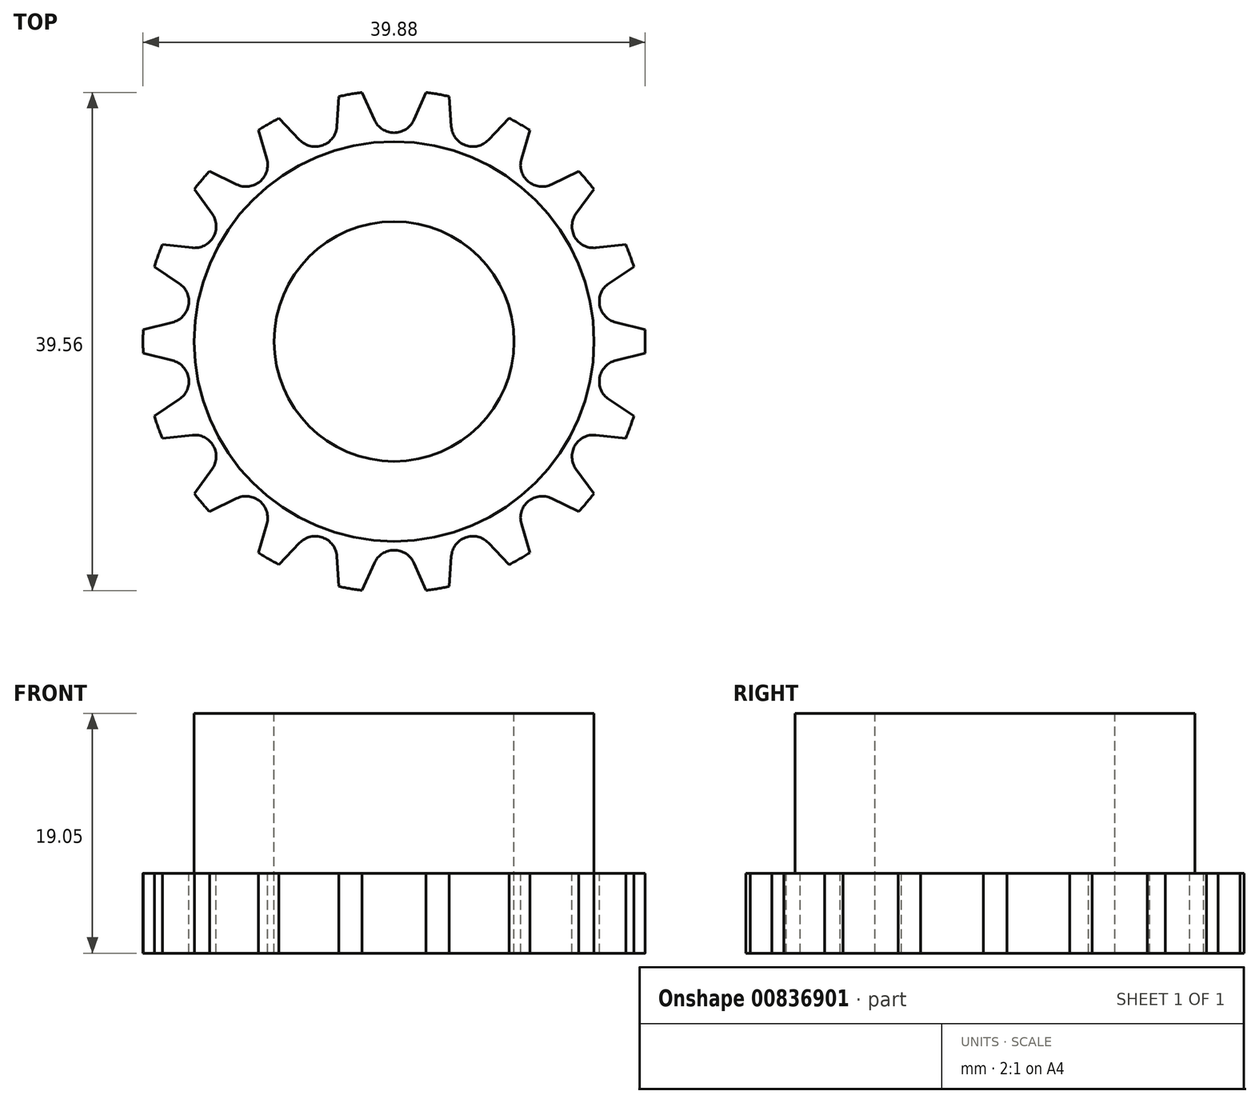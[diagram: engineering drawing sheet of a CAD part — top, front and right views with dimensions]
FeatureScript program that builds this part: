
annotation { "Feature Type Name" : "Feature", "Feature Type Description" : "" }
export const myFeature = defineFeature(function(context is Context, id is Id, definition is map)
    precondition{}
    {
        {
            var Q0;
            Q0=qCreatedBy(makeId("Top.planeOp"),FACE);
            var sketch = newSketch(context, id + "F0", { "sketchPlane" : qUnion([Q0])});
            skCircle(sketch, "E0", {"center": v(0, 0) * mm, "radius": 19.94 * mm});
            skSolve(sketch);
        }
        {
            var Q0;
            Q0=makeQuery(id+"F0.imprint","IMPRINT",FACE,{"disambiguationData":[TD([[makeQuery(id+"F0.imprint","IMPRINT",EDGE,{"derivedFrom":sQuery(id+"F0.wireOp",EDGE,"E0")}),1.0]])]});
            extrude(context, id + "F1", {"entities" : qUnion([Q0]), "depth" : 6.35 * mm, "offsetDistance" : 25.4 * mm});
        }
        {
            var Q0;
            Q0=makeQuery(id+"F1.opExtrude","CAP_FACE",FACE,{"disambiguationData":[OSD([sQuery(id+"F0.wireOp",EDGE,"E0")])],"isStart":false});
            var sketch = newSketch(context, id + "F2", { "sketchPlane" : qUnion([Q0])});
            skCircle(sketch, "E1", {"center": v(0, 0) * mm, "radius": 15.88 * mm});
            skSolve(sketch);
        }
        {
            var Q0;
            Q0 = qSketchRegion(id + "F2", true);
            extrude(context, id + "F3", {"entities" : qUnion([Q0]), "operationType" : NewBodyOperationType.ADD, "depth" : 12.7 * mm, "offsetDistance" : 25.4 * mm});
        }
        {
            var Q0;
            Q0=makeQuery(id+"F3.opExtrude","CAP_FACE",FACE,{"disambiguationData":[OSD([sQuery(id+"F2.wireOp",EDGE,"E1")])],"isStart":false});
            var sketch = newSketch(context, id + "F4", { "sketchPlane" : qUnion([Q0])});
            skCircle(sketch, "E2", {"center": v(0, 0) * mm, "radius": 9.53 * mm});
            skSolve(sketch);
        }
        {
            var Q0;
            Q0 = qSketchRegion(id + "F4", true);
            extrude(context, id + "F5", {"entities" : qUnion([Q0]), "operationType" : NewBodyOperationType.REMOVE, "oppositeDirection" : true, "depth" : 25.4 * mm, "offsetDistance" : 25.4 * mm});
        }
        {
            var Q0;
            Q0=makeQuery(id+"F1.opExtrude","CAP_FACE",FACE,{"disambiguationData":[OSD([sQuery(id+"F0.wireOp",EDGE,"E0")])],"isStart":false});
            var sketch = newSketch(context, id + "F6", { "sketchPlane" : qUnion([Q0])});
            skCircle(sketch, "E3", {"center": v(0, 0) * mm, "radius": 18.29 * mm, "construction": true});
            skArc(sketch, "E4", {"start": v(-1.57, 17.6) * mm, "mid": v(0, 16.57) * mm, "end": v(1.57, 17.6) * mm});
            skLineSegment(sketch, "E5", {"start": v(1.57, 17.6) * mm, "end": v(2.53, 19.78) * mm});
            skLineSegment(sketch, "E6", {"start": v(2.53, 19.78) * mm, "end": v(3.46, 19.62) * mm});
            skLineSegment(sketch, "E7", {"start": v(0, 18.29) * mm, "end": v(0, 21.23) * mm, "construction": true});
            skLineSegment(sketch, "E8", {"start": v(0, 0) * mm, "end": v(4.98, 28.27) * mm, "construction": true});
            skLineSegment(sketch, "E9.MirrorCS", {"start": v(-1.57, 17.6) * mm, "end": v(-2.53, 19.78) * mm});
            skLineSegment(sketch, "E10.MirrorCS", {"start": v(-2.53, 19.78) * mm, "end": v(-3.46, 19.62) * mm});
            skLineSegment(sketch, "E11", {"start": v(-3.46, 19.62) * mm, "end": v(-3.75, 21.29) * mm});
            skLineSegment(sketch, "E12", {"start": v(-3.75, 21.29) * mm, "end": v(5.38, 21.29) * mm});
            skLineSegment(sketch, "E13", {"start": v(5.38, 21.29) * mm, "end": v(3.46, 19.62) * mm});
            skLineSegment(sketch, "E14.1.0", {"start": v(-10.8, 18.72) * mm, "end": v(-2.22, 21.84) * mm});
            skLineSegment(sketch, "E14.1.1", {"start": v(-9.96, 17.25) * mm, "end": v(-10.8, 18.72) * mm});
            skLineSegment(sketch, "E14.1.2", {"start": v(-9.14, 17.72) * mm, "end": v(-9.96, 17.25) * mm});
            skLineSegment(sketch, "E14.1.3", {"start": v(-7.5, 16) * mm, "end": v(-9.14, 17.72) * mm});
            skArc(sketch, "E14.1.4", {"start": v(-7.5, 16) * mm, "mid": v(-5.67, 15.57) * mm, "end": v(-4.54, 17.07) * mm});
            skLineSegment(sketch, "E14.1.5", {"start": v(-4.54, 17.07) * mm, "end": v(-4.38, 19.45) * mm});
            skLineSegment(sketch, "E14.1.6", {"start": v(-4.38, 19.45) * mm, "end": v(-3.46, 19.62) * mm});
            skLineSegment(sketch, "E14.1.7", {"start": v(-2.22, 21.84) * mm, "end": v(-3.46, 19.62) * mm});
            skLineSegment(sketch, "E14.2.0", {"start": v(-16.56, 13.9) * mm, "end": v(-9.56, 19.77) * mm});
            skLineSegment(sketch, "E14.2.1", {"start": v(-15.26, 12.8) * mm, "end": v(-16.56, 13.9) * mm});
            skLineSegment(sketch, "E14.2.2", {"start": v(-14.65, 13.52) * mm, "end": v(-15.26, 12.8) * mm});
            skLineSegment(sketch, "E14.2.3", {"start": v(-12.51, 12.47) * mm, "end": v(-14.65, 13.52) * mm});
            skArc(sketch, "E14.2.4", {"start": v(-12.51, 12.47) * mm, "mid": v(-10.65, 12.7) * mm, "end": v(-10.1, 14.49) * mm});
            skLineSegment(sketch, "E14.2.5", {"start": v(-10.1, 14.49) * mm, "end": v(-10.77, 16.78) * mm});
            skLineSegment(sketch, "E14.2.6", {"start": v(-10.77, 16.78) * mm, "end": v(-9.96, 17.25) * mm});
            skLineSegment(sketch, "E14.2.7", {"start": v(-9.56, 19.77) * mm, "end": v(-9.96, 17.25) * mm});
            skLineSegment(sketch, "E14.3.0", {"start": v(-20.3, 7.4) * mm, "end": v(-15.74, 15.3) * mm});
            skLineSegment(sketch, "E14.3.1", {"start": v(-18.72, 6.81) * mm, "end": v(-20.3, 7.4) * mm});
            skLineSegment(sketch, "E14.3.2", {"start": v(-18.4, 7.7) * mm, "end": v(-18.72, 6.81) * mm});
            skLineSegment(sketch, "E14.3.3", {"start": v(-16.02, 7.44) * mm, "end": v(-18.4, 7.7) * mm});
            skArc(sketch, "E14.3.4", {"start": v(-16.02, 7.44) * mm, "mid": v(-14.35, 8.29) * mm, "end": v(-14.45, 10.16) * mm});
            skLineSegment(sketch, "E14.3.5", {"start": v(-14.45, 10.16) * mm, "end": v(-15.86, 12.08) * mm});
            skLineSegment(sketch, "E14.3.6", {"start": v(-15.86, 12.08) * mm, "end": v(-15.26, 12.8) * mm});
            skLineSegment(sketch, "E14.3.7", {"start": v(-15.74, 15.3) * mm, "end": v(-15.26, 12.8) * mm});
            skLineSegment(sketch, "E14.4.0", {"start": v(-21.61, 0) * mm, "end": v(-20.03, 9) * mm});
            skLineSegment(sketch, "E14.4.1", {"start": v(-19.92, 0) * mm, "end": v(-21.61, 0) * mm});
            skLineSegment(sketch, "E14.4.2", {"start": v(-19.92, 0.94) * mm, "end": v(-19.92, 0) * mm});
            skLineSegment(sketch, "E14.4.3", {"start": v(-17.6, 1.51) * mm, "end": v(-19.92, 0.94) * mm});
            skArc(sketch, "E14.4.4", {"start": v(-17.6, 1.51) * mm, "mid": v(-16.32, 2.88) * mm, "end": v(-17.05, 4.6) * mm});
            skLineSegment(sketch, "E14.4.5", {"start": v(-17.05, 4.6) * mm, "end": v(-19.04, 5.93) * mm});
            skLineSegment(sketch, "E14.4.6", {"start": v(-19.04, 5.93) * mm, "end": v(-18.72, 6.81) * mm});
            skLineSegment(sketch, "E14.4.7", {"start": v(-20.03, 9) * mm, "end": v(-18.72, 6.81) * mm});
            skLineSegment(sketch, "E14.5.0", {"start": v(-20.31, -7.4) * mm, "end": v(-21.9, 1.6) * mm});
            skLineSegment(sketch, "E14.5.1", {"start": v(-18.72, -6.81) * mm, "end": v(-20.31, -7.4) * mm});
            skLineSegment(sketch, "E14.5.2", {"start": v(-19.04, -5.93) * mm, "end": v(-18.72, -6.81) * mm});
            skLineSegment(sketch, "E14.5.3", {"start": v(-17.05, -4.6) * mm, "end": v(-19.04, -5.93) * mm});
            skArc(sketch, "E14.5.4", {"start": v(-17.05, -4.6) * mm, "mid": v(-16.32, -2.88) * mm, "end": v(-17.6, -1.51) * mm});
            skLineSegment(sketch, "E14.5.5", {"start": v(-17.6, -1.51) * mm, "end": v(-19.92, -0.94) * mm});
            skLineSegment(sketch, "E14.5.6", {"start": v(-19.92, -0.94) * mm, "end": v(-19.92, 0) * mm});
            skLineSegment(sketch, "E14.5.7", {"start": v(-21.9, 1.6) * mm, "end": v(-19.92, 0) * mm});
            skLineSegment(sketch, "E14.6.0", {"start": v(-16.56, -13.9) * mm, "end": v(-21.13, -5.98) * mm});
            skLineSegment(sketch, "E14.6.1", {"start": v(-15.26, -12.8) * mm, "end": v(-16.56, -13.9) * mm});
            skLineSegment(sketch, "E14.6.2", {"start": v(-15.86, -12.08) * mm, "end": v(-15.26, -12.8) * mm});
            skLineSegment(sketch, "E14.6.3", {"start": v(-14.45, -10.16) * mm, "end": v(-15.86, -12.08) * mm});
            skArc(sketch, "E14.6.4", {"start": v(-14.45, -10.16) * mm, "mid": v(-14.35, -8.29) * mm, "end": v(-16.02, -7.44) * mm});
            skLineSegment(sketch, "E14.6.5", {"start": v(-16.02, -7.44) * mm, "end": v(-18.4, -7.7) * mm});
            skLineSegment(sketch, "E14.6.6", {"start": v(-18.4, -7.7) * mm, "end": v(-18.72, -6.81) * mm});
            skLineSegment(sketch, "E14.6.7", {"start": v(-21.13, -5.98) * mm, "end": v(-18.72, -6.81) * mm});
            skLineSegment(sketch, "E14.7.0", {"start": v(-10.8, -18.72) * mm, "end": v(-17.8, -12.85) * mm});
            skLineSegment(sketch, "E14.7.1", {"start": v(-9.96, -17.25) * mm, "end": v(-10.8, -18.72) * mm});
            skLineSegment(sketch, "E14.7.2", {"start": v(-10.77, -16.78) * mm, "end": v(-9.96, -17.25) * mm});
            skLineSegment(sketch, "E14.7.3", {"start": v(-10.1, -14.49) * mm, "end": v(-10.77, -16.78) * mm});
            skArc(sketch, "E14.7.4", {"start": v(-10.1, -14.49) * mm, "mid": v(-10.65, -12.7) * mm, "end": v(-12.51, -12.47) * mm});
            skLineSegment(sketch, "E14.7.5", {"start": v(-12.51, -12.47) * mm, "end": v(-14.65, -13.52) * mm});
            skLineSegment(sketch, "E14.7.6", {"start": v(-14.65, -13.52) * mm, "end": v(-15.26, -12.8) * mm});
            skLineSegment(sketch, "E14.7.7", {"start": v(-17.8, -12.85) * mm, "end": v(-15.26, -12.8) * mm});
            skLineSegment(sketch, "E14.8.0", {"start": v(-3.75, -21.29) * mm, "end": v(-12.34, -18.16) * mm});
            skLineSegment(sketch, "E14.8.1", {"start": v(-3.46, -19.62) * mm, "end": v(-3.75, -21.29) * mm});
            skLineSegment(sketch, "E14.8.2", {"start": v(-4.38, -19.45) * mm, "end": v(-3.46, -19.62) * mm});
            skLineSegment(sketch, "E14.8.3", {"start": v(-4.54, -17.07) * mm, "end": v(-4.38, -19.45) * mm});
            skArc(sketch, "E14.8.4", {"start": v(-4.54, -17.07) * mm, "mid": v(-5.67, -15.57) * mm, "end": v(-7.5, -16) * mm});
            skLineSegment(sketch, "E14.8.5", {"start": v(-7.5, -16) * mm, "end": v(-9.14, -17.72) * mm});
            skLineSegment(sketch, "E14.8.6", {"start": v(-9.14, -17.72) * mm, "end": v(-9.96, -17.25) * mm});
            skLineSegment(sketch, "E14.8.7", {"start": v(-12.34, -18.16) * mm, "end": v(-9.96, -17.25) * mm});
            skLineSegment(sketch, "E14.9.0", {"start": v(3.75, -21.29) * mm, "end": v(-5.38, -21.29) * mm});
            skLineSegment(sketch, "E14.9.1", {"start": v(3.46, -19.62) * mm, "end": v(3.75, -21.29) * mm});
            skLineSegment(sketch, "E14.9.2", {"start": v(2.53, -19.78) * mm, "end": v(3.46, -19.62) * mm});
            skLineSegment(sketch, "E14.9.3", {"start": v(1.57, -17.6) * mm, "end": v(2.53, -19.78) * mm});
            skArc(sketch, "E14.9.4", {"start": v(1.57, -17.6) * mm, "mid": v(0, -16.57) * mm, "end": v(-1.57, -17.6) * mm});
            skLineSegment(sketch, "E14.9.5", {"start": v(-1.57, -17.6) * mm, "end": v(-2.53, -19.78) * mm});
            skLineSegment(sketch, "E14.9.6", {"start": v(-2.53, -19.78) * mm, "end": v(-3.46, -19.62) * mm});
            skLineSegment(sketch, "E14.9.7", {"start": v(-5.38, -21.29) * mm, "end": v(-3.46, -19.62) * mm});
            skLineSegment(sketch, "E14.10.0", {"start": v(10.8, -18.72) * mm, "end": v(2.22, -21.84) * mm});
            skLineSegment(sketch, "E14.10.1", {"start": v(9.96, -17.25) * mm, "end": v(10.8, -18.72) * mm});
            skLineSegment(sketch, "E14.10.2", {"start": v(9.14, -17.72) * mm, "end": v(9.96, -17.25) * mm});
            skLineSegment(sketch, "E14.10.3", {"start": v(7.5, -16) * mm, "end": v(9.14, -17.72) * mm});
            skArc(sketch, "E14.10.4", {"start": v(7.5, -16) * mm, "mid": v(5.67, -15.57) * mm, "end": v(4.54, -17.07) * mm});
            skLineSegment(sketch, "E14.10.5", {"start": v(4.54, -17.07) * mm, "end": v(4.38, -19.45) * mm});
            skLineSegment(sketch, "E14.10.6", {"start": v(4.38, -19.45) * mm, "end": v(3.46, -19.62) * mm});
            skLineSegment(sketch, "E14.10.7", {"start": v(2.22, -21.84) * mm, "end": v(3.46, -19.62) * mm});
            skLineSegment(sketch, "E14.11.0", {"start": v(16.56, -13.9) * mm, "end": v(9.56, -19.77) * mm});
            skLineSegment(sketch, "E14.11.1", {"start": v(15.26, -12.8) * mm, "end": v(16.56, -13.9) * mm});
            skLineSegment(sketch, "E14.11.2", {"start": v(14.65, -13.52) * mm, "end": v(15.26, -12.8) * mm});
            skLineSegment(sketch, "E14.11.3", {"start": v(12.51, -12.47) * mm, "end": v(14.65, -13.52) * mm});
            skArc(sketch, "E14.11.4", {"start": v(12.51, -12.47) * mm, "mid": v(10.65, -12.7) * mm, "end": v(10.1, -14.49) * mm});
            skLineSegment(sketch, "E14.11.5", {"start": v(10.1, -14.49) * mm, "end": v(10.77, -16.78) * mm});
            skLineSegment(sketch, "E14.11.6", {"start": v(10.77, -16.78) * mm, "end": v(9.96, -17.25) * mm});
            skLineSegment(sketch, "E14.11.7", {"start": v(9.56, -19.77) * mm, "end": v(9.96, -17.25) * mm});
            skLineSegment(sketch, "E14.12.0", {"start": v(20.3, -7.4) * mm, "end": v(15.74, -15.3) * mm});
            skLineSegment(sketch, "E14.12.1", {"start": v(18.72, -6.81) * mm, "end": v(20.3, -7.4) * mm});
            skLineSegment(sketch, "E14.12.2", {"start": v(18.4, -7.7) * mm, "end": v(18.72, -6.81) * mm});
            skLineSegment(sketch, "E14.12.3", {"start": v(16.02, -7.44) * mm, "end": v(18.4, -7.7) * mm});
            skArc(sketch, "E14.12.4", {"start": v(16.02, -7.44) * mm, "mid": v(14.35, -8.29) * mm, "end": v(14.45, -10.16) * mm});
            skLineSegment(sketch, "E14.12.5", {"start": v(14.45, -10.16) * mm, "end": v(15.86, -12.08) * mm});
            skLineSegment(sketch, "E14.12.6", {"start": v(15.86, -12.08) * mm, "end": v(15.26, -12.8) * mm});
            skLineSegment(sketch, "E14.12.7", {"start": v(15.74, -15.3) * mm, "end": v(15.26, -12.8) * mm});
            skLineSegment(sketch, "E14.13.0", {"start": v(21.61, 0) * mm, "end": v(20.03, -9) * mm});
            skLineSegment(sketch, "E14.13.1", {"start": v(19.92, 0) * mm, "end": v(21.61, 0) * mm});
            skLineSegment(sketch, "E14.13.2", {"start": v(19.92, -0.94) * mm, "end": v(19.92, 0) * mm});
            skLineSegment(sketch, "E14.13.3", {"start": v(17.6, -1.51) * mm, "end": v(19.92, -0.94) * mm});
            skArc(sketch, "E14.13.4", {"start": v(17.6, -1.51) * mm, "mid": v(16.32, -2.88) * mm, "end": v(17.05, -4.6) * mm});
            skLineSegment(sketch, "E14.13.5", {"start": v(17.05, -4.6) * mm, "end": v(19.04, -5.93) * mm});
            skLineSegment(sketch, "E14.13.6", {"start": v(19.04, -5.93) * mm, "end": v(18.72, -6.81) * mm});
            skLineSegment(sketch, "E14.13.7", {"start": v(20.03, -9) * mm, "end": v(18.72, -6.81) * mm});
            skLineSegment(sketch, "E14.14.0", {"start": v(20.31, 7.4) * mm, "end": v(21.9, -1.6) * mm});
            skLineSegment(sketch, "E14.14.1", {"start": v(18.72, 6.81) * mm, "end": v(20.31, 7.4) * mm});
            skLineSegment(sketch, "E14.14.2", {"start": v(19.04, 5.93) * mm, "end": v(18.72, 6.81) * mm});
            skLineSegment(sketch, "E14.14.3", {"start": v(17.05, 4.6) * mm, "end": v(19.04, 5.93) * mm});
            skArc(sketch, "E14.14.4", {"start": v(17.05, 4.6) * mm, "mid": v(16.32, 2.88) * mm, "end": v(17.6, 1.51) * mm});
            skLineSegment(sketch, "E14.14.5", {"start": v(17.6, 1.51) * mm, "end": v(19.92, 0.94) * mm});
            skLineSegment(sketch, "E14.14.6", {"start": v(19.92, 0.94) * mm, "end": v(19.92, 0) * mm});
            skLineSegment(sketch, "E14.14.7", {"start": v(21.9, -1.6) * mm, "end": v(19.92, 0) * mm});
            skLineSegment(sketch, "E14.15.0", {"start": v(16.56, 13.9) * mm, "end": v(21.13, 5.98) * mm});
            skLineSegment(sketch, "E14.15.1", {"start": v(15.26, 12.8) * mm, "end": v(16.56, 13.9) * mm});
            skLineSegment(sketch, "E14.15.2", {"start": v(15.86, 12.08) * mm, "end": v(15.26, 12.8) * mm});
            skLineSegment(sketch, "E14.15.3", {"start": v(14.45, 10.16) * mm, "end": v(15.86, 12.08) * mm});
            skArc(sketch, "E14.15.4", {"start": v(14.45, 10.16) * mm, "mid": v(14.35, 8.29) * mm, "end": v(16.02, 7.44) * mm});
            skLineSegment(sketch, "E14.15.5", {"start": v(16.02, 7.44) * mm, "end": v(18.4, 7.7) * mm});
            skLineSegment(sketch, "E14.15.6", {"start": v(18.4, 7.7) * mm, "end": v(18.72, 6.81) * mm});
            skLineSegment(sketch, "E14.15.7", {"start": v(21.13, 5.98) * mm, "end": v(18.72, 6.81) * mm});
            skLineSegment(sketch, "E14.16.0", {"start": v(10.8, 18.72) * mm, "end": v(17.8, 12.85) * mm});
            skLineSegment(sketch, "E14.16.1", {"start": v(9.96, 17.25) * mm, "end": v(10.8, 18.72) * mm});
            skLineSegment(sketch, "E14.16.2", {"start": v(10.77, 16.78) * mm, "end": v(9.96, 17.25) * mm});
            skLineSegment(sketch, "E14.16.3", {"start": v(10.1, 14.49) * mm, "end": v(10.77, 16.78) * mm});
            skArc(sketch, "E14.16.4", {"start": v(10.1, 14.49) * mm, "mid": v(10.65, 12.7) * mm, "end": v(12.51, 12.47) * mm});
            skLineSegment(sketch, "E14.16.5", {"start": v(12.51, 12.47) * mm, "end": v(14.65, 13.52) * mm});
            skLineSegment(sketch, "E14.16.6", {"start": v(14.65, 13.52) * mm, "end": v(15.26, 12.8) * mm});
            skLineSegment(sketch, "E14.16.7", {"start": v(17.8, 12.85) * mm, "end": v(15.26, 12.8) * mm});
            skLineSegment(sketch, "E14.17.0", {"start": v(3.75, 21.29) * mm, "end": v(12.34, 18.16) * mm});
            skLineSegment(sketch, "E14.17.1", {"start": v(3.46, 19.62) * mm, "end": v(3.75, 21.29) * mm});
            skLineSegment(sketch, "E14.17.2", {"start": v(4.38, 19.45) * mm, "end": v(3.46, 19.62) * mm});
            skLineSegment(sketch, "E14.17.3", {"start": v(4.54, 17.07) * mm, "end": v(4.38, 19.45) * mm});
            skArc(sketch, "E14.17.4", {"start": v(4.54, 17.07) * mm, "mid": v(5.67, 15.57) * mm, "end": v(7.5, 16) * mm});
            skLineSegment(sketch, "E14.17.5", {"start": v(7.5, 16) * mm, "end": v(9.14, 17.72) * mm});
            skLineSegment(sketch, "E14.17.6", {"start": v(9.14, 17.72) * mm, "end": v(9.96, 17.25) * mm});
            skLineSegment(sketch, "E14.17.7", {"start": v(12.34, 18.16) * mm, "end": v(9.96, 17.25) * mm});
            skSolve(sketch);
        }
        {
            var Q0;
            Q0=makeQuery(id+"F6.imprint","IMPRINT",FACE,{"disambiguationData":[TD([[makeQuery(id+"F6.imprint","IMPRINT",EDGE,{"derivedFrom":sQuery(id+"F6.wireOp",EDGE,"E4")}),1.0]])]});
            var Q1;
            {var subQ0=sQuery(id+"F6.wireOp",EDGE,"E14.17.3");Q1=makeQuery(id+"F6.imprint","IMPRINT",FACE,{"disambiguationData":[TD([[makeQuery(id+"F6.imprint","IMPRINT",EDGE,{"derivedFrom":subQ0}),-1.0]])]});}
            var Q2;
            {var subQ0=sQuery(id+"F6.wireOp",EDGE,"E14.16.3");Q2=makeQuery(id+"F6.imprint","IMPRINT",FACE,{"disambiguationData":[TD([[makeQuery(id+"F6.imprint","IMPRINT",EDGE,{"derivedFrom":subQ0}),-1.0]])]});}
            var Q3;
            {var subQ0=sQuery(id+"F6.wireOp",EDGE,"E14.15.3");Q3=makeQuery(id+"F6.imprint","IMPRINT",FACE,{"disambiguationData":[TD([[makeQuery(id+"F6.imprint","IMPRINT",EDGE,{"derivedFrom":subQ0}),-1.0]])]});}
            var Q4;
            {var subQ0=sQuery(id+"F6.wireOp",EDGE,"E14.14.3");Q4=makeQuery(id+"F6.imprint","IMPRINT",FACE,{"disambiguationData":[TD([[makeQuery(id+"F6.imprint","IMPRINT",EDGE,{"derivedFrom":subQ0}),-1.0]])]});}
            var Q5;
            {var subQ0=sQuery(id+"F6.wireOp",EDGE,"E14.13.3");Q5=makeQuery(id+"F6.imprint","IMPRINT",FACE,{"disambiguationData":[TD([[makeQuery(id+"F6.imprint","IMPRINT",EDGE,{"derivedFrom":subQ0}),-1.0]])]});}
            var Q6;
            {var subQ0=sQuery(id+"F6.wireOp",EDGE,"E14.12.3");Q6=makeQuery(id+"F6.imprint","IMPRINT",FACE,{"disambiguationData":[TD([[makeQuery(id+"F6.imprint","IMPRINT",EDGE,{"derivedFrom":subQ0}),-1.0]])]});}
            var Q7;
            {var subQ0=sQuery(id+"F6.wireOp",EDGE,"E14.11.3");Q7=makeQuery(id+"F6.imprint","IMPRINT",FACE,{"disambiguationData":[TD([[makeQuery(id+"F6.imprint","IMPRINT",EDGE,{"derivedFrom":subQ0}),-1.0]])]});}
            var Q8;
            {var subQ0=sQuery(id+"F6.wireOp",EDGE,"E14.10.3");Q8=makeQuery(id+"F6.imprint","IMPRINT",FACE,{"disambiguationData":[TD([[makeQuery(id+"F6.imprint","IMPRINT",EDGE,{"derivedFrom":subQ0}),-1.0]])]});}
            var Q9;
            {var subQ0=sQuery(id+"F6.wireOp",EDGE,"E14.9.3");Q9=makeQuery(id+"F6.imprint","IMPRINT",FACE,{"disambiguationData":[TD([[makeQuery(id+"F6.imprint","IMPRINT",EDGE,{"derivedFrom":subQ0}),-1.0]])]});}
            var Q10;
            {var subQ0=sQuery(id+"F6.wireOp",EDGE,"E14.8.3");Q10=makeQuery(id+"F6.imprint","IMPRINT",FACE,{"disambiguationData":[TD([[makeQuery(id+"F6.imprint","IMPRINT",EDGE,{"derivedFrom":subQ0}),-1.0]])]});}
            var Q11;
            {var subQ0=sQuery(id+"F6.wireOp",EDGE,"E14.7.3");Q11=makeQuery(id+"F6.imprint","IMPRINT",FACE,{"disambiguationData":[TD([[makeQuery(id+"F6.imprint","IMPRINT",EDGE,{"derivedFrom":subQ0}),-1.0]])]});}
            var Q12;
            {var subQ0=sQuery(id+"F6.wireOp",EDGE,"E14.6.3");Q12=makeQuery(id+"F6.imprint","IMPRINT",FACE,{"disambiguationData":[TD([[makeQuery(id+"F6.imprint","IMPRINT",EDGE,{"derivedFrom":subQ0}),-1.0]])]});}
            var Q13;
            {var subQ0=sQuery(id+"F6.wireOp",EDGE,"E14.5.3");Q13=makeQuery(id+"F6.imprint","IMPRINT",FACE,{"disambiguationData":[TD([[makeQuery(id+"F6.imprint","IMPRINT",EDGE,{"derivedFrom":subQ0}),-1.0]])]});}
            var Q14;
            {var subQ0=sQuery(id+"F6.wireOp",EDGE,"E14.4.3");Q14=makeQuery(id+"F6.imprint","IMPRINT",FACE,{"disambiguationData":[TD([[makeQuery(id+"F6.imprint","IMPRINT",EDGE,{"derivedFrom":subQ0}),-1.0]])]});}
            var Q15;
            {var subQ0=sQuery(id+"F6.wireOp",EDGE,"E14.3.3");Q15=makeQuery(id+"F6.imprint","IMPRINT",FACE,{"disambiguationData":[TD([[makeQuery(id+"F6.imprint","IMPRINT",EDGE,{"derivedFrom":subQ0}),-1.0]])]});}
            var Q16;
            {var subQ0=sQuery(id+"F6.wireOp",EDGE,"E14.2.3");Q16=makeQuery(id+"F6.imprint","IMPRINT",FACE,{"disambiguationData":[TD([[makeQuery(id+"F6.imprint","IMPRINT",EDGE,{"derivedFrom":subQ0}),-1.0]])]});}
            var Q17;
            {var subQ0=sQuery(id+"F6.wireOp",EDGE,"E14.1.3");Q17=makeQuery(id+"F6.imprint","IMPRINT",FACE,{"disambiguationData":[TD([[makeQuery(id+"F6.imprint","IMPRINT",EDGE,{"derivedFrom":subQ0}),-1.0]])]});}
            extrude(context, id + "F7", {"entities" : qUnion([Q0, Q1, Q2, Q3, Q4, Q5, Q6, Q7, Q8, Q9, Q10, Q11, Q12, Q13, Q14, Q15, Q16, Q17]), "operationType" : NewBodyOperationType.REMOVE, "oppositeDirection" : true, "depth" : 25.4 * mm, "offsetDistance" : 25.4 * mm});
        }
    });
